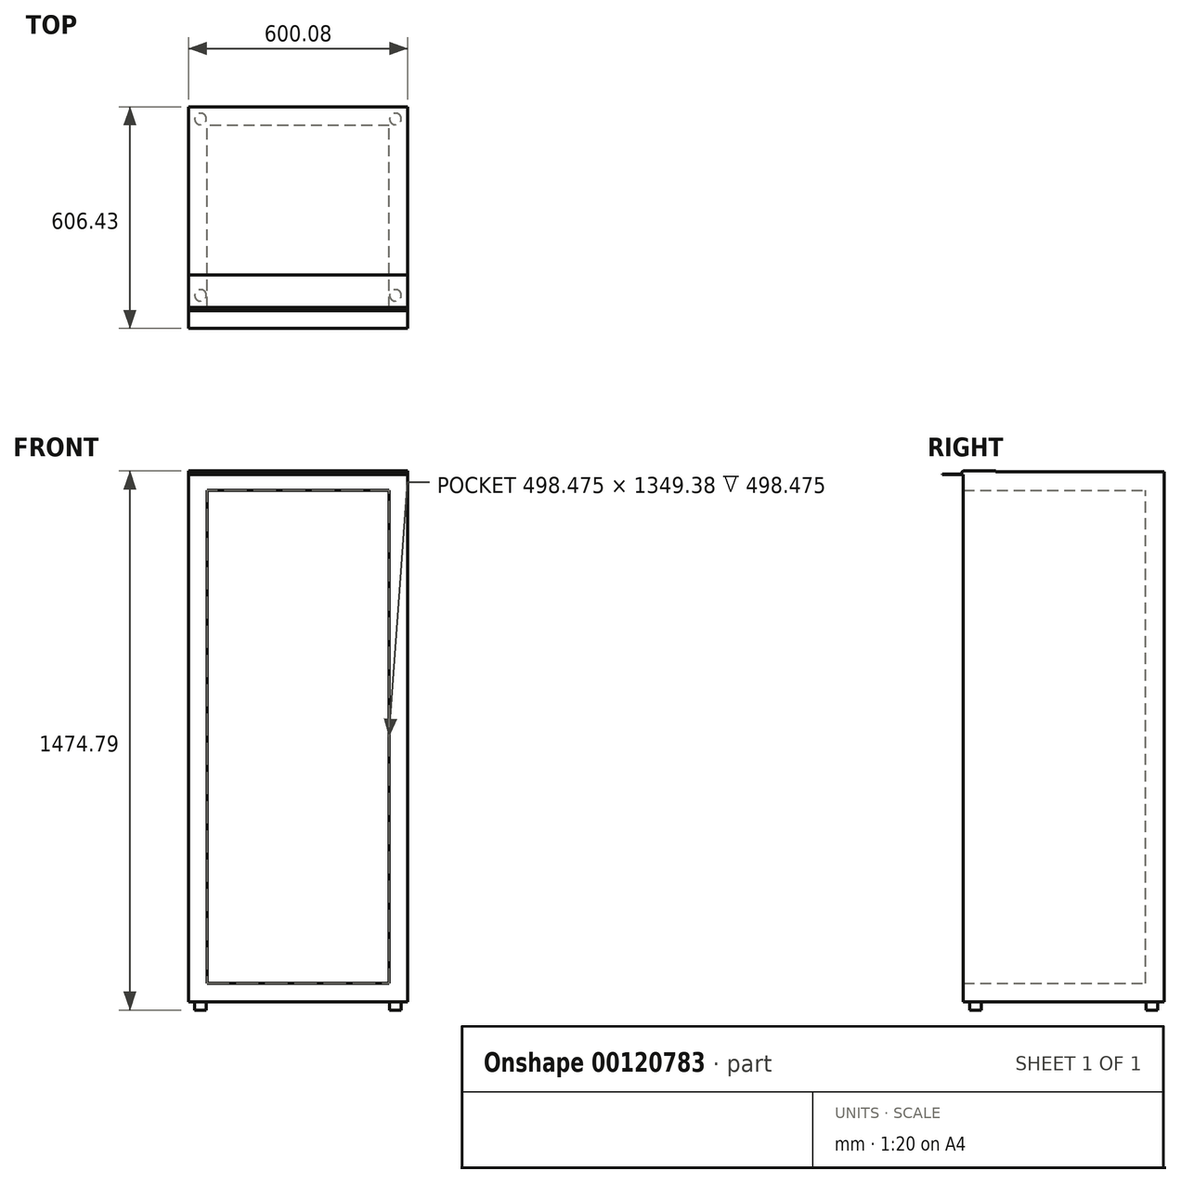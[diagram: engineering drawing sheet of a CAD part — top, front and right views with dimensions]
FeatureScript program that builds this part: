
annotation { "Feature Type Name" : "Feature", "Feature Type Description" : "" }
export const myFeature = defineFeature(function(context is Context, id is Id, definition is map)
    precondition{}
    {
        {
            var Q0;
            Q0=qCreatedBy(makeId("Front.planeOp"),FACE);
            var sketch = newSketch(context, id + "F0", { "sketchPlane" : qUnion([Q0])});
            skLineSegment(sketch, "E0.bottom", {"start": v(300.04, -725.49) * mm, "end": v(-300.04, -725.49) * mm});
            skLineSegment(sketch, "E0.top", {"start": v(300.04, 725.49) * mm, "end": v(-300.04, 725.49) * mm});
            skLineSegment(sketch, "E0.left", {"start": v(300.04, -725.49) * mm, "end": v(300.04, 725.49) * mm});
            skLineSegment(sketch, "E0.right", {"start": v(-300.04, -725.49) * mm, "end": v(-300.04, 725.49) * mm});
            skPoint(sketch, "E0.middle", {"position": v(0, 0) * mm});
            skSolve(sketch);
        }
        {
            var Q0;
            Q0=makeQuery(id+"F0.imprint","IMPRINT",FACE,{"disambiguationData":[TD([[makeQuery(id+"F0.imprint","IMPRINT",EDGE,{"derivedFrom":sQuery(id+"F0.wireOp",EDGE,"E0.bottom")}),-1.0]])]});
            extrude(context, id + "F1", {"entities" : qUnion([Q0]), "endBound" : BoundingType.SYMMETRIC, "depth" : 549.27 * mm});
        }
        {
            var Q0;
            Q0=makeQuery(id+"F1.opExtrude","CAP_FACE",FACE,{"disambiguationData":[OSD([sQuery(id+"F0.wireOp",EDGE,"E0.bottom"),sQuery(id+"F0.wireOp",EDGE,"E0.top"),sQuery(id+"F0.wireOp",EDGE,"E0.left"),sQuery(id+"F0.wireOp",EDGE,"E0.right")])],"isStart":false});
            shell(context, id + "F2", {"entities" : qUnion([Q0]), "thickness" : 50.8 * mm});
        }
        {
            var Q0;
            Q0=makeQuery(id+"F1.opExtrude","SWEPT_FACE",FACE,{"disambiguationData":[OSD([sQuery(id+"F0.wireOp",EDGE,"E0.bottom")])]});
            var sketch = newSketch(context, id + "F3", { "sketchPlane" : qUnion([Q0])});
            skLineSegment(sketch, "E1.bottom", {"start": v(266.7, -241.3) * mm, "end": v(-266.7, -241.3) * mm});
            skLineSegment(sketch, "E1.top", {"start": v(266.7, 241.3) * mm, "end": v(-266.7, 241.3) * mm});
            skLineSegment(sketch, "E1.left", {"start": v(266.7, -241.3) * mm, "end": v(266.7, 241.3) * mm});
            skLineSegment(sketch, "E1.right", {"start": v(-266.7, -241.3) * mm, "end": v(-266.7, 241.3) * mm});
            skPoint(sketch, "E1.middle", {"position": v(0, 0) * mm});
            skCircle(sketch, "E2", {"center": v(-266.7, 241.3) * mm, "radius": 15.88 * mm});
            skLineSegment(sketch, "E3", {"start": v(-31.55, 0) * mm, "end": v(29.58, 0) * mm});
            skLineSegment(sketch, "E4", {"start": v(0, 35.98) * mm, "end": v(0, -37.96) * mm});
            skCircle(sketch, "E5.MirrorC", {"center": v(266.7, 241.3) * mm, "radius": 15.88 * mm});
            skCircle(sketch, "E6.MirrorC", {"center": v(-266.7, -241.3) * mm, "radius": 15.88 * mm});
            skCircle(sketch, "E7.MirrorC", {"center": v(266.7, -241.3) * mm, "radius": 15.88 * mm});
            skSolve(sketch);
        }
        {
            var Q0;
            {var subQ0=sQuery(id+"F3.wireOp",EDGE,"E1.right");var subQ1=sQuery(id+"F3.wireOp",EDGE,"E1.top");var subQ2=makeQuery(id+"F3.imprint","INTERSECT",VERTEX,{"derivedFrom":[subQ1,subQ0]});Q0=makeQuery(id+"F3.imprint","IMPRINT",FACE,{"disambiguationData":[TD([[makeQuery(id+"F3.imprint","IMPRINT",EDGE,{"disambiguationData":[TD([[subQ2,1.0]])],"derivedFrom":subQ1}),-1.0]])]});}
            var Q1;
            {var subQ0=sQuery(id+"F3.wireOp",EDGE,"E1.right");var subQ1=sQuery(id+"F3.wireOp",EDGE,"E1.top");var subQ2=makeQuery(id+"F3.imprint","INTERSECT",VERTEX,{"derivedFrom":[subQ1,subQ0]});Q1=makeQuery(id+"F3.imprint","IMPRINT",FACE,{"disambiguationData":[TD([[makeQuery(id+"F3.imprint","IMPRINT",EDGE,{"disambiguationData":[TD([[subQ2,1.0]])],"derivedFrom":subQ1}),1.0]])]});}
            var Q2;
            {var subQ0=sQuery(id+"F3.wireOp",EDGE,"E1.left");var subQ1=sQuery(id+"F3.wireOp",EDGE,"E1.top");var subQ2=makeQuery(id+"F3.imprint","INTERSECT",VERTEX,{"derivedFrom":[subQ1,subQ0]});Q2=makeQuery(id+"F3.imprint","IMPRINT",FACE,{"disambiguationData":[TD([[makeQuery(id+"F3.imprint","IMPRINT",EDGE,{"disambiguationData":[TD([[subQ2,-1.0]])],"derivedFrom":subQ1}),1.0]])]});}
            var Q3;
            {var subQ0=sQuery(id+"F3.wireOp",EDGE,"E1.left");var subQ1=sQuery(id+"F3.wireOp",EDGE,"E1.top");var subQ2=makeQuery(id+"F3.imprint","INTERSECT",VERTEX,{"derivedFrom":[subQ1,subQ0]});Q3=makeQuery(id+"F3.imprint","IMPRINT",FACE,{"disambiguationData":[TD([[makeQuery(id+"F3.imprint","IMPRINT",EDGE,{"disambiguationData":[TD([[subQ2,-1.0]])],"derivedFrom":subQ1}),-1.0]])]});}
            var Q4;
            {var subQ0=sQuery(id+"F3.wireOp",EDGE,"E1.left");var subQ1=sQuery(id+"F3.wireOp",EDGE,"E1.bottom");var subQ2=makeQuery(id+"F3.imprint","INTERSECT",VERTEX,{"derivedFrom":[subQ1,subQ0]});Q4=makeQuery(id+"F3.imprint","IMPRINT",FACE,{"disambiguationData":[TD([[makeQuery(id+"F3.imprint","IMPRINT",EDGE,{"disambiguationData":[TD([[subQ2,-1.0]])],"derivedFrom":subQ1}),-1.0]])]});}
            var Q5;
            {var subQ0=sQuery(id+"F3.wireOp",EDGE,"E1.left");var subQ1=sQuery(id+"F3.wireOp",EDGE,"E1.bottom");var subQ2=makeQuery(id+"F3.imprint","INTERSECT",VERTEX,{"derivedFrom":[subQ1,subQ0]});Q5=makeQuery(id+"F3.imprint","IMPRINT",FACE,{"disambiguationData":[TD([[makeQuery(id+"F3.imprint","IMPRINT",EDGE,{"disambiguationData":[TD([[subQ2,-1.0]])],"derivedFrom":subQ1}),1.0]])]});}
            var Q6;
            {var subQ0=sQuery(id+"F3.wireOp",EDGE,"E1.right");var subQ1=sQuery(id+"F3.wireOp",EDGE,"E1.bottom");var subQ2=makeQuery(id+"F3.imprint","INTERSECT",VERTEX,{"derivedFrom":[subQ1,subQ0]});Q6=makeQuery(id+"F3.imprint","IMPRINT",FACE,{"disambiguationData":[TD([[makeQuery(id+"F3.imprint","IMPRINT",EDGE,{"disambiguationData":[TD([[subQ2,1.0]])],"derivedFrom":subQ1}),-1.0]])]});}
            var Q7;
            {var subQ0=sQuery(id+"F3.wireOp",EDGE,"E1.right");var subQ1=sQuery(id+"F3.wireOp",EDGE,"E1.bottom");var subQ2=makeQuery(id+"F3.imprint","INTERSECT",VERTEX,{"derivedFrom":[subQ1,subQ0]});Q7=makeQuery(id+"F3.imprint","IMPRINT",FACE,{"disambiguationData":[TD([[makeQuery(id+"F3.imprint","IMPRINT",EDGE,{"disambiguationData":[TD([[subQ2,1.0]])],"derivedFrom":subQ1}),1.0]])]});}
            extrude(context, id + "F4", {"entities" : qUnion([Q0, Q1, Q2, Q3, Q4, Q5, Q6, Q7]), "operationType" : NewBodyOperationType.ADD, "depth" : 22.22 * mm});
        }
        {
            var Q0;
            Q0=makeQuery(id+"F1.opExtrude","CAP_FACE",FACE,{"disambiguationData":[OSD([sQuery(id+"F0.wireOp",EDGE,"E0.bottom"),sQuery(id+"F0.wireOp",EDGE,"E0.top"),sQuery(id+"F0.wireOp",EDGE,"E0.left"),sQuery(id+"F0.wireOp",EDGE,"E0.right")])],"isStart":false});
            var sketch = newSketch(context, id + "F5", { "sketchPlane" : qUnion([Q0])});
            skLineSegment(sketch, "E8.bottom", {"start": v(-300.04, 717.55) * mm, "end": v(300.04, 717.55) * mm});
            skLineSegment(sketch, "E8.top", {"start": v(-300.04, 719.14) * mm, "end": v(300.04, 719.14) * mm});
            skLineSegment(sketch, "E8.left", {"start": v(-300.04, 717.55) * mm, "end": v(-300.04, 719.14) * mm});
            skLineSegment(sketch, "E8.right", {"start": v(300.04, 717.55) * mm, "end": v(300.04, 719.14) * mm});
            skPoint(sketch, "E8.middle", {"position": v(0, 718.34) * mm});
            skSolve(sketch);
        }
        {
            var Q0;
            Q0 = qSketchRegion(id + "F5", true);
            extrude(context, id + "F6", {"entities" : qUnion([Q0]), "operationType" : NewBodyOperationType.ADD, "depth" : 57.15 * mm});
        }
        {
            var Q0;
            Q0=makeQuery(id+"F1.opExtrude","SWEPT_FACE",FACE,{"disambiguationData":[OSD([sQuery(id+"F0.wireOp",EDGE,"E0.top")])]});
            var sketch = newSketch(context, id + "F7", { "sketchPlane" : qUnion([Q0])});
            skLineSegment(sketch, "E9.bottom", {"start": v(-300.04, -274.64) * mm, "end": v(300.04, -274.64) * mm});
            skLineSegment(sketch, "E9.top", {"start": v(-300.04, -185.74) * mm, "end": v(300.04, -185.74) * mm});
            skLineSegment(sketch, "E9.left", {"start": v(-300.04, -274.64) * mm, "end": v(-300.04, -185.74) * mm});
            skLineSegment(sketch, "E9.right", {"start": v(300.04, -274.64) * mm, "end": v(300.04, -185.74) * mm});
            skSolve(sketch);
        }
        {
            var Q0;
            Q0 = qSketchRegion(id + "F7", true);
            extrude(context, id + "F8", {"entities" : qUnion([Q0]), "operationType" : NewBodyOperationType.ADD, "depth" : 1.59 * mm});
        }
        {
            var Q0;
            Q0=makeQuery(id+"F8.boolean.opBoolean","MERGE",FACE,{"derivedFrom":[makeQuery(id+"F6.boolean.opBoolean","MERGE",FACE,{"derivedFrom":[makeQuery(id+"F1.opExtrude","SWEPT_FACE",FACE,{"disambiguationData":[OSD([sQuery(id+"F0.wireOp",EDGE,"E0.left")])]}),makeQuery(id+"F6.opExtrude","SWEPT_FACE",FACE,{"disambiguationData":[OSD([sQuery(id+"F5.wireOp",EDGE,"E8.right")])]})]}),makeQuery(id+"F8.opExtrude","SWEPT_FACE",FACE,{"disambiguationData":[OSD([sQuery(id+"F7.wireOp",EDGE,"E9.right")])]})]});
            var sketch = newSketch(context, id + "F9", { "sketchPlane" : qUnion([Q0])});
            skLineSegment(sketch, "E10", {"start": v(-274.64, 727.08) * mm, "end": v(-283.24, 719.14) * mm});
            skSolve(sketch);
        }
        {
            var Q0;
            Q0 = qSketchRegion(id + "F9", true);
            var Q1;
            {var subQ0=sQuery(id+"F9.wireOp",EDGE,"E10");Q1=makeQuery(id+"F9.imprint","IMPRINT",FACE,{"disambiguationData":[TD([[makeQuery(id+"F9.imprint","IMPRINT",EDGE,{"derivedFrom":subQ0}),1.0]])]});}
            extrude(context, id + "F10", {"entities" : qUnion([Q0, Q1]), "operationType" : NewBodyOperationType.ADD, "oppositeDirection" : true, "depth" : 600.07 * mm});
        }
    });
